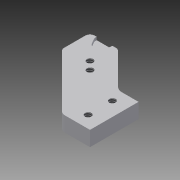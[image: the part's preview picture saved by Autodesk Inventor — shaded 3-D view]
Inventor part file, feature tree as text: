
AUTODESK INVENTOR PART (.ipt)
format: ipt  version: 2014 (Build 180170000, 170)  size: 120,320 bytes
history: native  units: in
note: dims shown in document units (in); Inventor stores cm internally (conversion verified against a paired STEP export)
features: other x3, plane x2
ambient origin geometry x8: Origin, YZ Plane, XZ Plane, XY Plane, X Axis, Y Axis, Z Axis, Center Point
bodies: Solid1 (feature_tree)
feature tree (5):
  other  "hph_A_001.ipt"
  other  "Solid2::hph_A_001.ipt"
  other  "TaggingFeature1"
  plane  "Work Plane1"
  plane  "Work Plane2"
